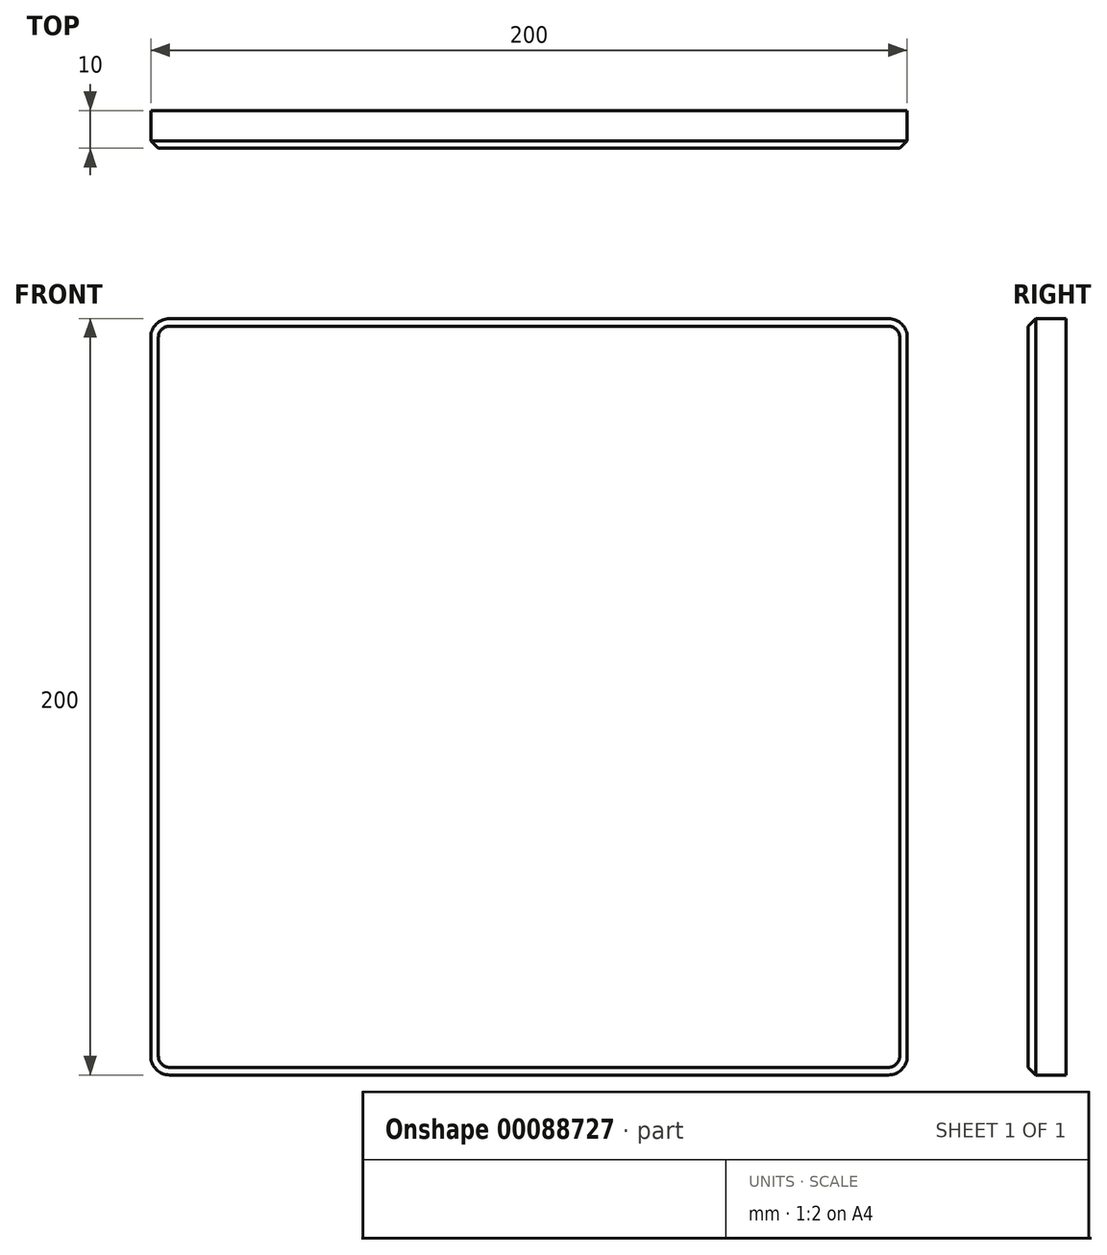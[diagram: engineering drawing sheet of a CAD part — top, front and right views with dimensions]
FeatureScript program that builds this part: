
annotation { "Feature Type Name" : "Feature", "Feature Type Description" : "" }
export const myFeature = defineFeature(function(context is Context, id is Id, definition is map)
    precondition{}
    {
        {
            var Q0;
            Q0=qCreatedBy(makeId("Front.planeOp"),FACE);
            var sketch = newSketch(context, id + "F0", { "sketchPlane" : qUnion([Q0])});
            skLineSegment(sketch, "E0.bottom", {"start": v(-100, 100) * mm, "end": v(100, 100) * mm});
            skLineSegment(sketch, "E0.top", {"start": v(-100, -100) * mm, "end": v(100, -100) * mm});
            skLineSegment(sketch, "E0.left", {"start": v(-100, 100) * mm, "end": v(-100, -100) * mm});
            skLineSegment(sketch, "E0.right", {"start": v(100, 100) * mm, "end": v(100, -100) * mm});
            skPoint(sketch, "E0.middle", {"position": v(0, 0) * mm});
            skSolve(sketch);
        }
        {
            var Q0;
            Q0 = qSketchRegion(id + "F0", true);
            var Q1;
            Q1=makeQuery(id+"F0.imprint","IMPRINT",FACE,{"disambiguationData":[TD([[makeQuery(id+"F0.imprint","IMPRINT",EDGE,{"derivedFrom":sQuery(id+"F0.wireOp",EDGE,"E0.bottom")}),-1.0]])]});
            extrude(context, id + "F1", {"entities" : qUnion([Q0, Q1]), "depth" : 10 * mm});
        }
        {
            var Q0;
            Q0=makeQuery(id+"F1.opExtrude","SWEPT_EDGE",EDGE,{"disambiguationData":[OSD([sQuery(id+"F0.wireOp",EDGE,"E0.top"),sQuery(id+"F0.wireOp",EDGE,"E0.right")])]});
            var Q1;
            Q1=makeQuery(id+"F1.opExtrude","SWEPT_EDGE",EDGE,{"disambiguationData":[OSD([sQuery(id+"F0.wireOp",EDGE,"E0.top"),sQuery(id+"F0.wireOp",EDGE,"E0.left")])]});
            var Q2;
            Q2=makeQuery(id+"F1.opExtrude","SWEPT_EDGE",EDGE,{"disambiguationData":[OSD([sQuery(id+"F0.wireOp",EDGE,"E0.bottom"),sQuery(id+"F0.wireOp",EDGE,"E0.left")])]});
            var Q3;
            Q3=makeQuery(id+"F1.opExtrude","SWEPT_EDGE",EDGE,{"disambiguationData":[OSD([sQuery(id+"F0.wireOp",EDGE,"E0.bottom"),sQuery(id+"F0.wireOp",EDGE,"E0.right")])]});
            fillet(context, id + "F2", {"entities" : qUnion([Q0, Q1, Q2, Q3]), "radius" : 5 * mm, "tangentPropagation" : true, "allowEdgeOverflow" : false});
        }
        {
            var Q0;
            Q0=makeQuery(id+"F1.opExtrude","CAP_FACE",FACE,{"disambiguationData":[OSD([sQuery(id+"F0.wireOp",EDGE,"E0.bottom"),sQuery(id+"F0.wireOp",EDGE,"E0.top"),sQuery(id+"F0.wireOp",EDGE,"E0.left"),sQuery(id+"F0.wireOp",EDGE,"E0.right")])],"isStart":false});
            chamfer(context, id + "F3", {"entities" : qUnion([Q0]), "width" : 2 * mm, "tangentPropagation" : true});
        }
    });
